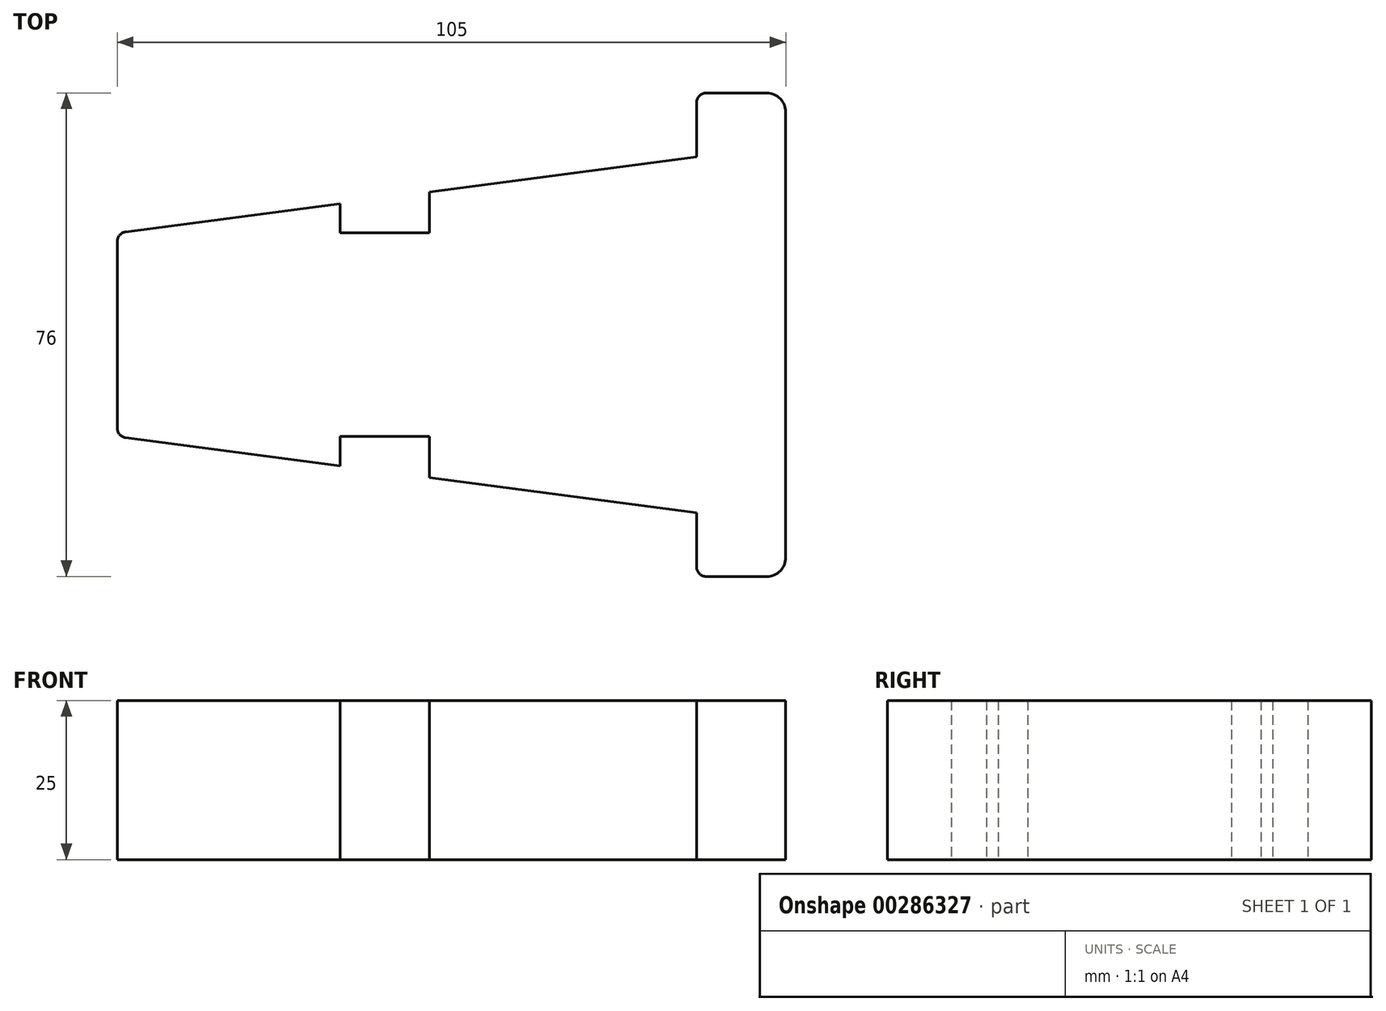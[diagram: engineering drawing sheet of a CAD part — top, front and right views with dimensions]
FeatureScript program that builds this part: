
annotation { "Feature Type Name" : "Feature", "Feature Type Description" : "" }
export const myFeature = defineFeature(function(context is Context, id is Id, definition is map)
    precondition{}
    {
        {
            var Q0;
            Q0=qCreatedBy(makeId("Top.planeOp"),FACE);
            var sketch = newSketch(context, id + "F0", { "sketchPlane" : qUnion([Q0])});
            skLineSegment(sketch, "E0", {"start": v(28.5, 28.4) * mm, "end": v(28.5, -41.6) * mm});
            skLineSegment(sketch, "E1", {"start": v(28.5, -44.6) * mm, "end": v(14.5, -44.6) * mm});
            skLineSegment(sketch, "E2", {"start": v(14.5, -43.1) * mm, "end": v(14.5, -34.6) * mm});
            skLineSegment(sketch, "E3", {"start": v(25.5, 31.4) * mm, "end": v(16, 31.4) * mm});
            skLineSegment(sketch, "E4", {"start": v(14.5, 29.9) * mm, "end": v(14.5, 21.4) * mm});
            skLineSegment(sketch, "E5", {"start": v(25.5, -44.6) * mm, "end": v(16, -44.6) * mm, "construction": true});
            skPoint(sketch, "E5.endSnap0", {"position": v(21.5, -44.6) * mm});
            skLineSegment(sketch, "E6", {"start": v(-76.5, -44.6) * mm, "end": v(-76.5, -22.6) * mm, "construction": true});
            skLineSegment(sketch, "E7", {"start": v(-76.5, -21.28) * mm, "end": v(-76.5, 8.1) * mm});
            skLineSegment(sketch, "E8", {"start": v(-76.5, 9.4) * mm, "end": v(-41.5, 14.02) * mm});
            skLineSegment(sketch, "E9", {"start": v(-75.2, -22.77) * mm, "end": v(-41.5, -27.2) * mm});
            skLineSegment(sketch, "E10", {"start": v(-75.2, 9.58) * mm, "end": v(-41.5, 14.02) * mm});
            skLineSegment(sketch, "E11", {"start": v(-41.5, 14.02) * mm, "end": v(-41.5, 9.4) * mm});
            skLineSegment(sketch, "E12", {"start": v(-27.5, 9.4) * mm, "end": v(-27.5, 15.87) * mm});
            skLineSegment(sketch, "E13.trimOffspring", {"start": v(-27.5, 15.87) * mm, "end": v(14.5, 21.4) * mm});
            skLineSegment(sketch, "E14", {"start": v(-76.5, -22.6) * mm, "end": v(-41.5, -27.2) * mm});
            skPoint(sketch, "E15.end.orphan", {"position": v(-31, -28.6) * mm});
            skLineSegment(sketch, "E16", {"start": v(-27.5, -29.06) * mm, "end": v(-27.5, -22.6) * mm});
            skLineSegment(sketch, "E17", {"start": v(-41.5, -22.6) * mm, "end": v(-41.5, -27.2) * mm});
            skLineSegment(sketch, "E18.trimOffspring", {"start": v(-27.5, -29.06) * mm, "end": v(14.5, -34.6) * mm});
            skLineSegment(sketch, "E19", {"start": v(-41.5, 9.4) * mm, "end": v(-27.5, 9.4) * mm});
            skLineSegment(sketch, "E20", {"start": v(-41.5, -22.6) * mm, "end": v(-27.5, -22.6) * mm});
            skLineSegment(sketch, "E21", {"start": v(-41.5, -27.2) * mm, "end": v(-41.5, -22.6) * mm});
            skLineSegment(sketch, "E22", {"start": v(-41.5, 9.4) * mm, "end": v(-41.5, 14.02) * mm});
            skPoint(sketch, "E23.orphan", {"position": v(-41.5, 6.47) * mm});
            skPoint(sketch, "E24.orphan", {"position": v(-27.5, 6.47) * mm});
            skPoint(sketch, "E25.orphan", {"position": v(-27.5, -20.92) * mm});
            skPoint(sketch, "E26.orphan", {"position": v(-41.5, -20.92) * mm});
            skPoint(sketch, "E27.orphan", {"position": v(-25.36, 9.4) * mm});
            skPoint(sketch, "E28.visualSharp", {"position": v(-76.5, 9.4) * mm});
            skArc(sketch, "E28.filletArc", {"start": v(-75.2, 9.58) * mm, "mid": v(-76.12, 9.08) * mm, "end": v(-76.5, 8.1) * mm});
            skPoint(sketch, "E29.visualSharp", {"position": v(-76.5, -22.6) * mm});
            skArc(sketch, "E29.filletArc", {"start": v(-76.5, -21.28) * mm, "mid": v(-76.12, -22.27) * mm, "end": v(-75.2, -22.77) * mm});
            skPoint(sketch, "E30.visualSharp", {"position": v(14.5, 31.4) * mm});
            skArc(sketch, "E30.filletArc", {"start": v(16, 31.4) * mm, "mid": v(14.94, 30.97) * mm, "end": v(14.5, 29.9) * mm});
            skPoint(sketch, "E31.newPointA", {"position": v(14.5, -44.6) * mm});
            skPoint(sketch, "E31.newPointB", {"position": v(-76.5, -44.6) * mm});
            skArc(sketch, "E31.filletArc", {"start": v(14.5, -43.1) * mm, "mid": v(14.94, -44.15) * mm, "end": v(16, -44.6) * mm});
            skPoint(sketch, "E32.visualSharp", {"position": v(28.5, 31.4) * mm});
            skArc(sketch, "E32.filletArc", {"start": v(28.5, 28.4) * mm, "mid": v(27.63, 30.53) * mm, "end": v(25.5, 31.4) * mm});
            skPoint(sketch, "E33.visualSharp", {"position": v(28.5, -44.6) * mm});
            skArc(sketch, "E33.filletArc", {"start": v(25.5, -44.6) * mm, "mid": v(27.63, -43.72) * mm, "end": v(28.5, -41.6) * mm});
            skSolve(sketch);
        }
        {
            var Q0;
            Q0 = qSketchRegion(id + "F0", true);
            extrude(context, id + "F1", {"entities" : qUnion([Q0]), "depth" : 25 * mm});
        }
    });
